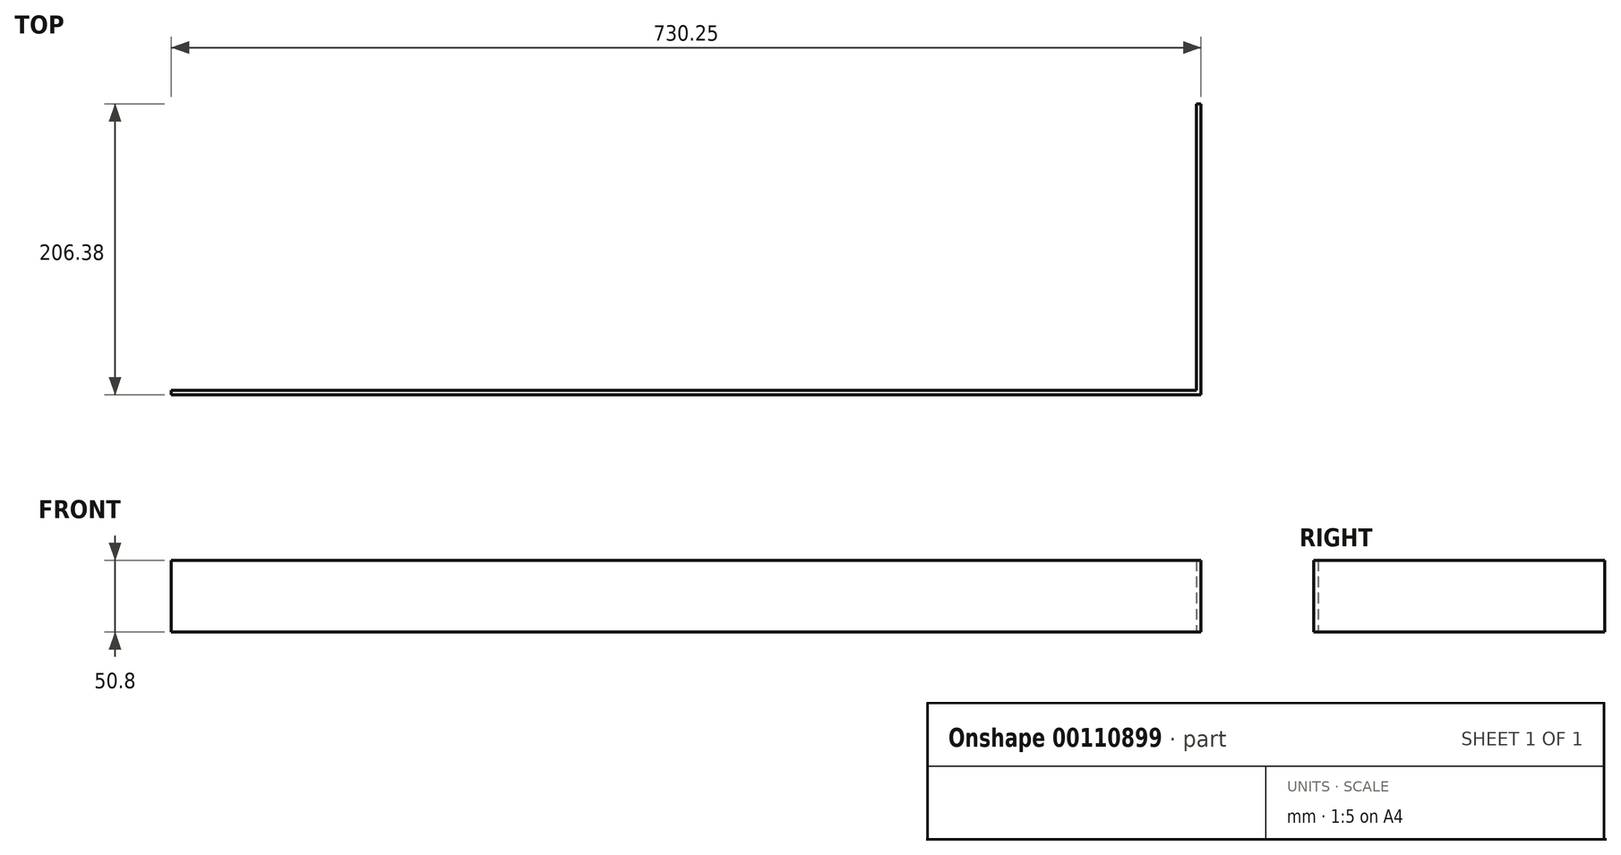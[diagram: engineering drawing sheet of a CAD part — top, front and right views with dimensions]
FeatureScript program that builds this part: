
annotation { "Feature Type Name" : "Feature", "Feature Type Description" : "" }
export const myFeature = defineFeature(function(context is Context, id is Id, definition is map)
    precondition{}
    {
        {
            var Q0;
            Q0=qCreatedBy(makeId("Top.planeOp"),FACE);
            var sketch = newSketch(context, id + "F0", { "sketchPlane" : qUnion([Q0])});
            skLineSegment(sketch, "E0.bottom", {"start": v(0, 0) * mm, "end": v(730.25, 0) * mm});
            skLineSegment(sketch, "E0.top", {"start": v(0, 3.18) * mm, "end": v(727.08, 3.18) * mm});
            skLineSegment(sketch, "E0.left", {"start": v(0, 0) * mm, "end": v(0, 3.18) * mm});
            skLineSegment(sketch, "E0.right", {"start": v(730.25, 0) * mm, "end": v(730.25, 3.18) * mm});
            skLineSegment(sketch, "E1.top", {"start": v(730.25, 206.38) * mm, "end": v(727.08, 206.38) * mm});
            skLineSegment(sketch, "E1.left", {"start": v(730.25, 3.17) * mm, "end": v(730.25, 206.38) * mm});
            skLineSegment(sketch, "E1.right", {"start": v(727.08, 3.18) * mm, "end": v(727.08, 206.38) * mm});
            skSolve(sketch);
        }
        {
            var Q0;
            Q0 = qSketchRegion(id + "F0", true);
            extrude(context, id + "F1", {"entities" : qUnion([Q0]), "depth" : 50.8 * mm});
        }
    });
